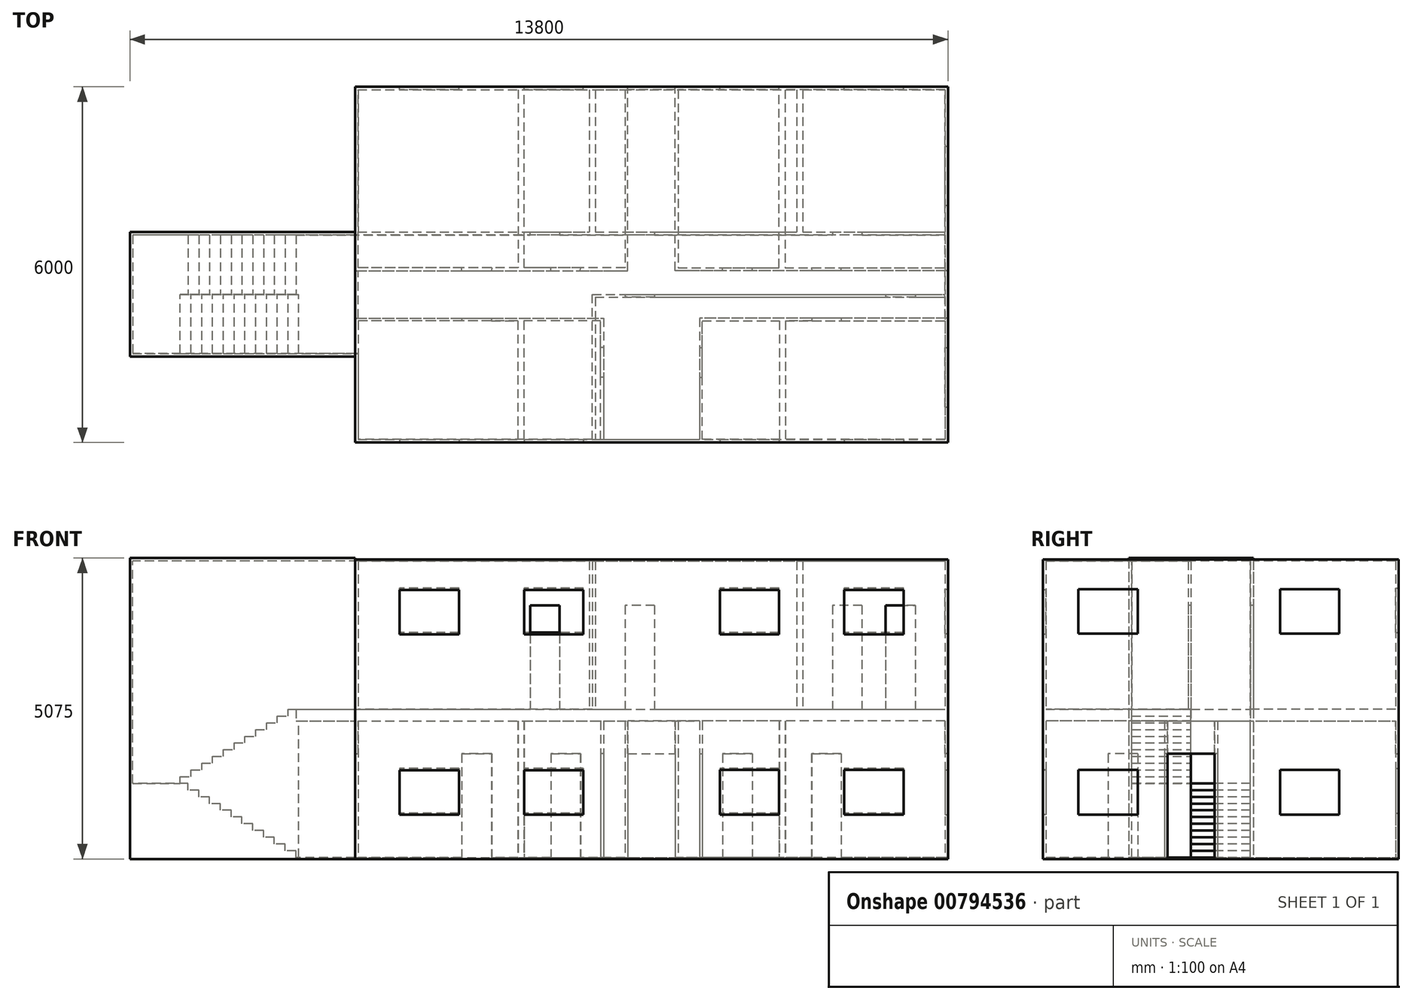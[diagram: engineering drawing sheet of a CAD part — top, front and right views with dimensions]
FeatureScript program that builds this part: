
annotation { "Feature Type Name" : "Feature", "Feature Type Description" : "" }
export const myFeature = defineFeature(function(context is Context, id is Id, definition is map)
    precondition{}
    {
        {
            var Q0;
            Q0=qCreatedBy(makeId("Top.planeOp"),FACE);
            var sketch = newSketch(context, id + "F0", { "sketchPlane" : qUnion([Q0])});
            skLineSegment(sketch, "E0.bottom", {"start": v(0, 0) * mm, "end": v(10000, 0) * mm});
            skLineSegment(sketch, "E0.top", {"start": v(0, 6000) * mm, "end": v(10000, 6000) * mm});
            skLineSegment(sketch, "E0.left", {"start": v(0, 0) * mm, "end": v(0, 6000) * mm});
            skLineSegment(sketch, "E0.right", {"start": v(10000, 0) * mm, "end": v(10000, 6000) * mm});
            skSolve(sketch);
        }
        {
            var Q0;
            Q0=qCreatedBy(makeId("Top.planeOp"),FACE);
            var sketch = newSketch(context, id + "F1", { "sketchPlane" : qUnion([Q0])});
            skLineSegment(sketch, "E1.bottom", {"start": v(0, 0) * mm, "end": v(5000, 0) * mm});
            skLineSegment(sketch, "E1.top", {"start": v(0, 6000) * mm, "end": v(4600, 6000) * mm});
            skLineSegment(sketch, "E1.left", {"start": v(0, 0) * mm, "end": v(0, 2100) * mm});
            skLineSegment(sketch, "E2", {"start": v(0, 2900) * mm, "end": v(1800, 2900) * mm});
            skLineSegment(sketch, "E3", {"start": v(0, 2100) * mm, "end": v(1800, 2100) * mm});
            skLineSegment(sketch, "E4", {"start": v(2800, 2900) * mm, "end": v(2800, 6000) * mm});
            skLineSegment(sketch, "E5", {"start": v(2792.35, 2100) * mm, "end": v(2792.35, 0) * mm});
            skLineSegment(sketch, "E6", {"start": v(2800, 2900) * mm, "end": v(3300, 2900) * mm});
            skLineSegment(sketch, "E7", {"start": v(4600, 2900) * mm, "end": v(4600, 6000) * mm});
            skLineSegment(sketch, "E8", {"start": v(2792.35, 2100) * mm, "end": v(4192.35, 2100) * mm});
            skLineSegment(sketch, "E9", {"start": v(4192.35, 2100) * mm, "end": v(4192.35, 1600) * mm});
            skPoint(sketch, "E10", {"position": v(1800, 2900) * mm});
            skPoint(sketch, "E11", {"position": v(2300, 2900) * mm});
            skPoint(sketch, "E12", {"position": v(1800, 2100) * mm});
            skPoint(sketch, "E13", {"position": v(2300, 2100) * mm});
            skPoint(sketch, "E14", {"position": v(4192.35, 1600) * mm});
            skPoint(sketch, "E15", {"position": v(3300, 2900) * mm});
            skPoint(sketch, "E16", {"position": v(3800, 2900) * mm});
            skPoint(sketch, "E17", {"position": v(4192.35, 1100) * mm});
            skLineSegment(sketch, "E18.trimOffspring", {"start": v(2300, 2900) * mm, "end": v(2800, 2900) * mm});
            skLineSegment(sketch, "E19.trimOffspring", {"start": v(2300, 2100) * mm, "end": v(2792.35, 2100) * mm});
            skLineSegment(sketch, "E20.trimOffspring", {"start": v(3800, 2900) * mm, "end": v(4600, 2900) * mm});
            skLineSegment(sketch, "E21.trimOffspring", {"start": v(4192.35, 1100) * mm, "end": v(4192.35, 0) * mm});
            skLineSegment(sketch, "E22.trimOffspring", {"start": v(0, 2900) * mm, "end": v(0, 6000) * mm});
            skLineSegment(sketch, "E23", {"start": v(1800, 2100) * mm, "end": v(1800, 2050) * mm});
            skLineSegment(sketch, "E24", {"start": v(1800, 2050) * mm, "end": v(50, 2050) * mm});
            skLineSegment(sketch, "E25", {"start": v(50, 2050) * mm, "end": v(50, 50) * mm});
            skLineSegment(sketch, "E26", {"start": v(50, 50) * mm, "end": v(2742.35, 50) * mm});
            skLineSegment(sketch, "E27", {"start": v(2300, 2100) * mm, "end": v(2300, 2050) * mm});
            skLineSegment(sketch, "E28", {"start": v(2300, 2050) * mm, "end": v(2742.35, 2050) * mm});
            skLineSegment(sketch, "E29", {"start": v(2742.35, 2050) * mm, "end": v(2742.35, 50) * mm});
            skLineSegment(sketch, "E30", {"start": v(4192.35, 1600) * mm, "end": v(4142.35, 1600) * mm});
            skLineSegment(sketch, "E31", {"start": v(4142.35, 1600) * mm, "end": v(4142.35, 2050) * mm});
            skLineSegment(sketch, "E32", {"start": v(4142.35, 2050) * mm, "end": v(2842.35, 2050) * mm});
            skLineSegment(sketch, "E33", {"start": v(2842.35, 2050) * mm, "end": v(2842.35, 50) * mm});
            skLineSegment(sketch, "E34", {"start": v(2842.35, 50) * mm, "end": v(4142.35, 50) * mm});
            skLineSegment(sketch, "E35", {"start": v(4192.35, 1100) * mm, "end": v(4142.35, 1100) * mm});
            skLineSegment(sketch, "E36", {"start": v(4142.35, 50) * mm, "end": v(4142.35, 1100) * mm});
            skLineSegment(sketch, "E37", {"start": v(4192.35, 50) * mm, "end": v(5000, 50) * mm});
            skLineSegment(sketch, "E38", {"start": v(5000, 0) * mm, "end": v(5000, 50) * mm});
            skLineSegment(sketch, "E39", {"start": v(1800, 2900) * mm, "end": v(1800, 2950) * mm});
            skLineSegment(sketch, "E40", {"start": v(1800, 2950) * mm, "end": v(50, 2950) * mm});
            skLineSegment(sketch, "E41", {"start": v(50, 2950) * mm, "end": v(50, 5950) * mm});
            skLineSegment(sketch, "E42", {"start": v(50, 5950) * mm, "end": v(2750, 5950) * mm});
            skLineSegment(sketch, "E43", {"start": v(2750, 5950) * mm, "end": v(2750, 2950) * mm});
            skLineSegment(sketch, "E44", {"start": v(2750, 2950) * mm, "end": v(2303.7, 2950) * mm});
            skLineSegment(sketch, "E45", {"start": v(2303.7, 2950) * mm, "end": v(2300, 2900) * mm});
            skLineSegment(sketch, "E46", {"start": v(3300, 2900) * mm, "end": v(3300, 2950) * mm});
            skLineSegment(sketch, "E47", {"start": v(3300, 2950) * mm, "end": v(2850, 2950) * mm});
            skLineSegment(sketch, "E48", {"start": v(2850, 2950) * mm, "end": v(2850, 5950) * mm});
            skLineSegment(sketch, "E49", {"start": v(2850, 5950) * mm, "end": v(4550, 5950) * mm});
            skLineSegment(sketch, "E50", {"start": v(4550, 5950) * mm, "end": v(4550, 2950) * mm});
            skLineSegment(sketch, "E51", {"start": v(4550, 2950) * mm, "end": v(3800.9, 2950) * mm});
            skLineSegment(sketch, "E52", {"start": v(3800, 2900) * mm, "end": v(3800.9, 2950) * mm});
            skSolve(sketch);
        }
        {
            var Q0;
            Q0=qSketchRegion(id+"F0",true);
            extrude(context, id + "F2", {"entities" : qUnion([Q0]), "oppositeDirection" : true, "depth" : 25 * mm, "offsetDistance" : 25 * mm});
        }
        {
            var Q0;
            Q0=qSketchRegion(id+"F1",true);
            extrude(context, id + "F3", {"entities" : qUnion([Q0]), "operationType" : NewBodyOperationType.ADD, "depth" : 2500 * mm, "offsetDistance" : 25 * mm});
        }
        {
            var Q0;
            Q0=qCreatedBy(makeId("Top.planeOp"),FACE);
            cPlane(context, id + "F4", {"entities" : qUnion([Q0]), "cplaneType" : CPlaneType.OFFSET, "offset" : 2500 * mm, "width" : 150 * mm, "height" : 150 * mm});
        }
        {
            var Q0;
            Q0=qCreatedBy(id+"F4.planeOp",FACE);
            var sketch = newSketch(context, id + "F5", { "sketchPlane" : qUnion([Q0])});
            skLineSegment(sketch, "E53.bottom", {"start": v(0, 0) * mm, "end": v(10000, 0) * mm});
            skLineSegment(sketch, "E53.top", {"start": v(0, 6000) * mm, "end": v(10000, 6000) * mm});
            skLineSegment(sketch, "E53.left", {"start": v(0, 0) * mm, "end": v(0, 6000) * mm});
            skLineSegment(sketch, "E53.right", {"start": v(10000, 0) * mm, "end": v(10000, 6000) * mm});
            skSolve(sketch);
        }
        {
            var Q0;
            Q0=qSketchRegion(id+"F5",true);
            extrude(context, id + "F6", {"entities" : qUnion([Q0]), "operationType" : NewBodyOperationType.ADD, "oppositeDirection" : true, "depth" : 200 * mm, "offsetDistance" : 25 * mm});
        }
        {
            var Q0;
            Q0=qCreatedBy(id+"F4.planeOp",FACE);
            var sketch = newSketch(context, id + "F7", { "sketchPlane" : qUnion([Q0])});
            skLineSegment(sketch, "E54.bottom", {"start": v(0, 0) * mm, "end": v(5000, 0) * mm});
            skLineSegment(sketch, "E54.top", {"start": v(0, 6000) * mm, "end": v(4600, 6000) * mm});
            skLineSegment(sketch, "E54.left", {"start": v(0, 0) * mm, "end": v(0, 2100) * mm});
            skLineSegment(sketch, "E55", {"start": v(0, 2900) * mm, "end": v(1800, 2900) * mm});
            skLineSegment(sketch, "E56", {"start": v(0, 2100) * mm, "end": v(1800, 2100) * mm});
            skLineSegment(sketch, "E57", {"start": v(2800, 2900) * mm, "end": v(2800, 6000) * mm});
            skLineSegment(sketch, "E58", {"start": v(2792.35, 2100) * mm, "end": v(2792.35, 0) * mm});
            skLineSegment(sketch, "E59", {"start": v(2800, 2900) * mm, "end": v(3300, 2900) * mm});
            skLineSegment(sketch, "E60", {"start": v(4600, 2900) * mm, "end": v(4600, 6000) * mm});
            skLineSegment(sketch, "E61", {"start": v(2792.35, 2100) * mm, "end": v(4192.35, 2100) * mm});
            skLineSegment(sketch, "E62", {"start": v(4192.35, 2100) * mm, "end": v(4192.35, 1600) * mm});
            skPoint(sketch, "E63", {"position": v(1800, 2900) * mm});
            skPoint(sketch, "E64", {"position": v(2300, 2900) * mm});
            skPoint(sketch, "E65", {"position": v(1800, 2100) * mm});
            skPoint(sketch, "E66", {"position": v(2300, 2100) * mm});
            skPoint(sketch, "E67", {"position": v(4192.35, 1600) * mm});
            skPoint(sketch, "E68", {"position": v(3300, 2900) * mm});
            skPoint(sketch, "E69", {"position": v(3800, 2900) * mm});
            skPoint(sketch, "E70", {"position": v(4192.35, 1100) * mm});
            skLineSegment(sketch, "E71.trimOffspring", {"start": v(2300, 2900) * mm, "end": v(2800, 2900) * mm});
            skLineSegment(sketch, "E72.trimOffspring", {"start": v(2300, 2100) * mm, "end": v(2792.35, 2100) * mm});
            skLineSegment(sketch, "E73.trimOffspring", {"start": v(3800, 2900) * mm, "end": v(4600, 2900) * mm});
            skLineSegment(sketch, "E74.trimOffspring", {"start": v(4192.35, 1100) * mm, "end": v(4192.35, 0) * mm});
            skLineSegment(sketch, "E75.trimOffspring", {"start": v(0, 2900) * mm, "end": v(0, 6000) * mm});
            skLineSegment(sketch, "E76", {"start": v(1800, 2100) * mm, "end": v(1800, 2050) * mm});
            skLineSegment(sketch, "E77", {"start": v(1800, 2050) * mm, "end": v(50, 2050) * mm});
            skLineSegment(sketch, "E78", {"start": v(50, 2050) * mm, "end": v(50, 50) * mm});
            skLineSegment(sketch, "E79", {"start": v(50, 50) * mm, "end": v(2742.35, 50) * mm});
            skLineSegment(sketch, "E80", {"start": v(2300, 2100) * mm, "end": v(2300, 2050) * mm});
            skLineSegment(sketch, "E81", {"start": v(2300, 2050) * mm, "end": v(2742.35, 2050) * mm});
            skLineSegment(sketch, "E82", {"start": v(2742.35, 2050) * mm, "end": v(2742.35, 50) * mm});
            skLineSegment(sketch, "E83", {"start": v(4192.35, 1600) * mm, "end": v(4142.35, 1600) * mm});
            skLineSegment(sketch, "E84", {"start": v(4142.35, 1600) * mm, "end": v(4142.35, 2050) * mm});
            skLineSegment(sketch, "E85", {"start": v(4142.35, 2050) * mm, "end": v(2842.35, 2050) * mm});
            skLineSegment(sketch, "E86", {"start": v(2842.35, 2050) * mm, "end": v(2842.35, 50) * mm});
            skLineSegment(sketch, "E87", {"start": v(2842.35, 50) * mm, "end": v(4142.35, 50) * mm});
            skLineSegment(sketch, "E88", {"start": v(4192.35, 1100) * mm, "end": v(4142.35, 1100) * mm});
            skLineSegment(sketch, "E89", {"start": v(4142.35, 50) * mm, "end": v(4142.35, 1100) * mm});
            skLineSegment(sketch, "E90", {"start": v(4192.35, 50) * mm, "end": v(5000, 50) * mm});
            skLineSegment(sketch, "E91", {"start": v(5000, 0) * mm, "end": v(5000, 50) * mm});
            skLineSegment(sketch, "E92", {"start": v(1800, 2900) * mm, "end": v(1800, 2950) * mm});
            skLineSegment(sketch, "E93", {"start": v(1800, 2950) * mm, "end": v(50, 2950) * mm});
            skLineSegment(sketch, "E94", {"start": v(50, 2950) * mm, "end": v(50, 5950) * mm});
            skLineSegment(sketch, "E95", {"start": v(50, 5950) * mm, "end": v(2750, 5950) * mm});
            skLineSegment(sketch, "E96", {"start": v(2750, 5950) * mm, "end": v(2750, 2950) * mm});
            skLineSegment(sketch, "E97", {"start": v(2750, 2950) * mm, "end": v(2303.7, 2950) * mm});
            skLineSegment(sketch, "E98", {"start": v(2303.7, 2950) * mm, "end": v(2300, 2900) * mm});
            skLineSegment(sketch, "E99", {"start": v(3300, 2900) * mm, "end": v(3300, 2950) * mm});
            skLineSegment(sketch, "E100", {"start": v(3300, 2950) * mm, "end": v(2850, 2950) * mm});
            skLineSegment(sketch, "E101", {"start": v(2850, 2950) * mm, "end": v(2850, 5950) * mm});
            skLineSegment(sketch, "E102", {"start": v(2850, 5950) * mm, "end": v(4550, 5950) * mm});
            skLineSegment(sketch, "E103", {"start": v(4550, 5950) * mm, "end": v(4550, 2950) * mm});
            skLineSegment(sketch, "E104", {"start": v(4550, 2950) * mm, "end": v(3800.9, 2950) * mm});
            skLineSegment(sketch, "E105", {"start": v(3800, 2900) * mm, "end": v(3800.9, 2950) * mm});
            skLineSegment(sketch, "E106", {"start": v(0, 2900) * mm, "end": v(0, 2100) * mm});
            skLineSegment(sketch, "E107", {"start": v(50, 2050) * mm, "end": v(50, 2950) * mm});
            skLineSegment(sketch, "E108", {"start": v(1800, 2050) * mm, "end": v(2300, 2050) * mm});
            skLineSegment(sketch, "E109", {"start": v(2300, 2100) * mm, "end": v(1800, 2100) * mm});
            skLineSegment(sketch, "E110", {"start": v(1800, 2900) * mm, "end": v(2300, 2900) * mm});
            skLineSegment(sketch, "E111", {"start": v(1800, 2950) * mm, "end": v(2303.7, 2950) * mm});
            skLineSegment(sketch, "E112", {"start": v(3300, 2900) * mm, "end": v(3800, 2900) * mm});
            skLineSegment(sketch, "E113", {"start": v(3800.9, 2950) * mm, "end": v(3300, 2950) * mm});
            skLineSegment(sketch, "E114", {"start": v(4192.35, 1600) * mm, "end": v(4192.35, 1100) * mm});
            skLineSegment(sketch, "E115", {"start": v(4142.35, 1100) * mm, "end": v(4142.35, 1600) * mm});
            skLineSegment(sketch, "E116", {"start": v(4600, 6000) * mm, "end": v(5000, 6000) * mm});
            skLineSegment(sketch, "E117", {"start": v(5000, 6000) * mm, "end": v(5000, 5950) * mm});
            skLineSegment(sketch, "E118", {"start": v(5000, 5950) * mm, "end": v(4550, 5950) * mm});
            skSolve(sketch);
        }
        {
            var Q0;
            Q0=qSketchRegion(id+"F7",true);
            extrude(context, id + "F8", {"entities" : qUnion([Q0]), "operationType" : NewBodyOperationType.ADD, "oppositeDirection" : true, "depth" : 750 * mm, "offsetDistance" : 25 * mm});
        }
        {
            var Q0;
            Q0=makeQuery(id+"F2.opExtrude","SWEPT_BODY",BODY,{"disambiguationData":[OSD([sQuery(id+"F0.wireOp",EDGE,"E0.bottom"),sQuery(id+"F0.wireOp",EDGE,"E0.top"),sQuery(id+"F0.wireOp",EDGE,"E0.left"),sQuery(id+"F0.wireOp",EDGE,"E0.right")])]});
            var Q1;
            Q1=makeQuery(id+"F3.opExtrude","SWEPT_FACE",FACE,{"disambiguationData":[OSD([sQuery(id+"F1.wireOp",EDGE,"E38")])]});
            mirror(context, id + "F9", {"operationType" : NewBodyOperationType.ADD, "entities" : qUnion([Q0]), "mirrorPlane" : qUnion([Q1])});
        }
        {
            var Q0;
            Q0=qCreatedBy(makeId("Front.planeOp"),FACE);
            cPlane(context, id + "F10", {"entities" : qUnion([Q0]), "cplaneType" : CPlaneType.OFFSET, "offset" : 2500 * mm, "oppositeDirection" : true, "width" : 150 * mm, "height" : 150 * mm});
        }
        {
            var Q0;
            Q0=qCreatedBy(id+"F10.planeOp",FACE);
            var sketch = newSketch(context, id + "F11", { "sketchPlane" : qUnion([Q0])});
            skLineSegment(sketch, "E119.bottom", {"start": v(-1000, 0) * mm, "end": v(-3000, 0) * mm});
            skLineSegment(sketch, "E119.right", {"start": v(-3000, 0) * mm, "end": v(-3000, 1250) * mm});
            skLineSegment(sketch, "E120", {"start": v(-1000, 0) * mm, "end": v(-3000, 1250) * mm});
            skLineSegment(sketch, "E121.bottom", {"start": v(-1000, 0) * mm, "end": v(-1181.82, 0) * mm});
            skLineSegment(sketch, "E121.top", {"start": v(-1000, 113.64) * mm, "end": v(-1181.82, 113.64) * mm});
            skLineSegment(sketch, "E121.left", {"start": v(-1000, 0) * mm, "end": v(-1000, 113.64) * mm});
            skLineSegment(sketch, "E121.right", {"start": v(-1181.82, 0) * mm, "end": v(-1181.82, 113.64) * mm});
            skLineSegment(sketch, "E122.bottom", {"start": v(-1181.82, 0) * mm, "end": v(-1363.64, 0) * mm});
            skLineSegment(sketch, "E122.top", {"start": v(-1181.82, 227.27) * mm, "end": v(-1363.64, 227.27) * mm});
            skLineSegment(sketch, "E122.left", {"start": v(-1181.82, 0) * mm, "end": v(-1181.82, 227.27) * mm});
            skLineSegment(sketch, "E122.right", {"start": v(-1363.64, 0) * mm, "end": v(-1363.64, 227.27) * mm});
            skLineSegment(sketch, "E123.bottom", {"start": v(-1363.64, 0) * mm, "end": v(-1545.45, 0) * mm});
            skLineSegment(sketch, "E123.top", {"start": v(-1363.64, 340.9) * mm, "end": v(-1545.45, 340.9) * mm});
            skLineSegment(sketch, "E123.left", {"start": v(-1363.64, 0) * mm, "end": v(-1363.64, 340.9) * mm});
            skLineSegment(sketch, "E123.right", {"start": v(-1545.45, 0) * mm, "end": v(-1545.45, 340.9) * mm});
            skLineSegment(sketch, "E124.bottom", {"start": v(-1545.45, 0) * mm, "end": v(-1727.27, 0) * mm});
            skLineSegment(sketch, "E124.top", {"start": v(-1545.45, 454.55) * mm, "end": v(-1727.27, 454.55) * mm});
            skLineSegment(sketch, "E124.left", {"start": v(-1545.45, 0) * mm, "end": v(-1545.45, 454.55) * mm});
            skLineSegment(sketch, "E124.right", {"start": v(-1727.27, 0) * mm, "end": v(-1727.27, 454.55) * mm});
            skLineSegment(sketch, "E125.bottom", {"start": v(-1727.27, 0) * mm, "end": v(-1909.1, 0) * mm});
            skLineSegment(sketch, "E125.top", {"start": v(-1727.27, 568.18) * mm, "end": v(-1909.1, 568.18) * mm});
            skLineSegment(sketch, "E125.left", {"start": v(-1727.27, 0) * mm, "end": v(-1727.27, 568.18) * mm});
            skLineSegment(sketch, "E125.right", {"start": v(-1909.1, 0) * mm, "end": v(-1909.1, 568.18) * mm});
            skLineSegment(sketch, "E126.bottom", {"start": v(-1909.1, 0) * mm, "end": v(-2090.9, 0) * mm});
            skLineSegment(sketch, "E126.top", {"start": v(-1909.1, 681.81) * mm, "end": v(-2090.9, 681.81) * mm});
            skLineSegment(sketch, "E126.left", {"start": v(-1909.1, 0) * mm, "end": v(-1909.1, 681.81) * mm});
            skLineSegment(sketch, "E126.right", {"start": v(-2090.9, 0) * mm, "end": v(-2090.9, 681.81) * mm});
            skLineSegment(sketch, "E127.bottom", {"start": v(-2090.9, 0) * mm, "end": v(-2272.72, 0) * mm});
            skLineSegment(sketch, "E127.top", {"start": v(-2090.9, 795.45) * mm, "end": v(-2272.72, 795.45) * mm});
            skLineSegment(sketch, "E127.left", {"start": v(-2090.9, 0) * mm, "end": v(-2090.9, 795.45) * mm});
            skLineSegment(sketch, "E127.right", {"start": v(-2272.72, 0) * mm, "end": v(-2272.72, 795.45) * mm});
            skLineSegment(sketch, "E128.bottom", {"start": v(-2272.72, 0) * mm, "end": v(-2454.54, 0) * mm});
            skLineSegment(sketch, "E128.top", {"start": v(-2272.72, 909.09) * mm, "end": v(-2454.54, 909.09) * mm});
            skLineSegment(sketch, "E128.left", {"start": v(-2272.72, 0) * mm, "end": v(-2272.72, 909.09) * mm});
            skLineSegment(sketch, "E128.right", {"start": v(-2454.54, 0) * mm, "end": v(-2454.54, 909.09) * mm});
            skLineSegment(sketch, "E129.bottom", {"start": v(-2454.54, 0) * mm, "end": v(-2636.36, 0) * mm});
            skLineSegment(sketch, "E129.top", {"start": v(-2454.54, 1022.72) * mm, "end": v(-2636.36, 1022.72) * mm});
            skLineSegment(sketch, "E129.left", {"start": v(-2454.54, 0) * mm, "end": v(-2454.54, 1022.72) * mm});
            skLineSegment(sketch, "E129.right", {"start": v(-2636.36, 0) * mm, "end": v(-2636.36, 1022.72) * mm});
            skLineSegment(sketch, "E130.bottom", {"start": v(-2636.36, 0) * mm, "end": v(-2818.17, 0) * mm});
            skLineSegment(sketch, "E130.top", {"start": v(-2636.36, 1136.36) * mm, "end": v(-2818.17, 1136.36) * mm});
            skLineSegment(sketch, "E130.left", {"start": v(-2636.36, 0) * mm, "end": v(-2636.36, 1136.36) * mm});
            skLineSegment(sketch, "E130.right", {"start": v(-2818.17, 0) * mm, "end": v(-2818.17, 1136.36) * mm});
            skLineSegment(sketch, "E131.bottom", {"start": v(-3000, 0) * mm, "end": v(-3750, 0) * mm});
            skLineSegment(sketch, "E131.top", {"start": v(-3000, 1250) * mm, "end": v(-3750, 1250) * mm});
            skLineSegment(sketch, "E131.right", {"start": v(-3750, 0) * mm, "end": v(-3750, 1250) * mm});
            skLineSegment(sketch, "E132.bottom", {"start": v(-2818.17, 0) * mm, "end": v(-3000, 0) * mm});
            skLineSegment(sketch, "E132.top", {"start": v(-2818.17, 1250) * mm, "end": v(-3000, 1250) * mm});
            skLineSegment(sketch, "E132.left", {"start": v(-2818.17, 0) * mm, "end": v(-2818.17, 1250) * mm});
            skSolve(sketch);
        }
        {
            var Q0;
            Q0=qSketchRegion(id+"F11",true);
            extrude(context, id + "F12", {"entities" : qUnion([Q0]), "operationType" : NewBodyOperationType.ADD, "oppositeDirection" : true, "depth" : 1000 * mm, "offsetDistance" : 25 * mm});
        }
        {
            var Q0;
            Q0=qCreatedBy(id+"F10.planeOp",FACE);
            var sketch = newSketch(context, id + "F13", { "sketchPlane" : qUnion([Q0])});
            skLineSegment(sketch, "E133.bottom", {"start": v(-3750, 0) * mm, "end": v(-2950, 0) * mm});
            skLineSegment(sketch, "E133.top", {"start": v(-3750, 1250) * mm, "end": v(-2950, 1250) * mm});
            skLineSegment(sketch, "E133.left", {"start": v(-3750, 0) * mm, "end": v(-3750, 1250) * mm});
            skLineSegment(sketch, "E133.right", {"start": v(-2950, 0) * mm, "end": v(-2950, 1250) * mm});
            skLineSegment(sketch, "E134", {"start": v(-2950, 1250) * mm, "end": v(-950, 1250) * mm});
            skLineSegment(sketch, "E135", {"start": v(-2950, 0) * mm, "end": v(-950, 0) * mm});
            skLineSegment(sketch, "E136", {"start": v(-950, 0) * mm, "end": v(-950, 1250) * mm});
            skLineSegment(sketch, "E137", {"start": v(-950, 1250) * mm, "end": v(-950, 2500) * mm});
            skLineSegment(sketch, "E138", {"start": v(-2950, 1250) * mm, "end": v(-950, 2500) * mm});
            skLineSegment(sketch, "E139.bottom", {"start": v(-2950, 1250) * mm, "end": v(-2768.18, 1250) * mm});
            skLineSegment(sketch, "E139.top", {"start": v(-2950, 1363.64) * mm, "end": v(-2768.18, 1363.64) * mm});
            skLineSegment(sketch, "E139.left", {"start": v(-2950, 1250) * mm, "end": v(-2950, 1363.64) * mm});
            skLineSegment(sketch, "E139.right", {"start": v(-2768.18, 1250) * mm, "end": v(-2768.18, 1363.64) * mm});
            skLineSegment(sketch, "E140.bottom", {"start": v(-2768.18, 1250) * mm, "end": v(-2586.36, 1250) * mm});
            skLineSegment(sketch, "E140.top", {"start": v(-2768.18, 1477.27) * mm, "end": v(-2586.36, 1477.27) * mm});
            skLineSegment(sketch, "E140.left", {"start": v(-2768.18, 1250) * mm, "end": v(-2768.18, 1477.27) * mm});
            skLineSegment(sketch, "E140.right", {"start": v(-2586.36, 1250) * mm, "end": v(-2586.36, 1477.27) * mm});
            skLineSegment(sketch, "E141.bottom", {"start": v(-2586.36, 1250) * mm, "end": v(-2404.55, 1250) * mm});
            skLineSegment(sketch, "E141.top", {"start": v(-2586.36, 1590.9) * mm, "end": v(-2404.55, 1590.9) * mm});
            skLineSegment(sketch, "E141.left", {"start": v(-2586.36, 1250) * mm, "end": v(-2586.36, 1590.9) * mm});
            skLineSegment(sketch, "E141.right", {"start": v(-2404.55, 1250) * mm, "end": v(-2404.55, 1590.9) * mm});
            skLineSegment(sketch, "E142.bottom", {"start": v(-2404.55, 1250) * mm, "end": v(-2222.74, 1250) * mm});
            skLineSegment(sketch, "E142.top", {"start": v(-2404.55, 1704.54) * mm, "end": v(-2222.74, 1704.54) * mm});
            skLineSegment(sketch, "E142.left", {"start": v(-2404.55, 1250) * mm, "end": v(-2404.55, 1704.54) * mm});
            skLineSegment(sketch, "E142.right", {"start": v(-2222.74, 1250) * mm, "end": v(-2222.74, 1704.54) * mm});
            skLineSegment(sketch, "E143.bottom", {"start": v(-2222.74, 1250) * mm, "end": v(-2040.92, 1250) * mm});
            skLineSegment(sketch, "E143.top", {"start": v(-2222.74, 1818.18) * mm, "end": v(-2040.92, 1818.18) * mm});
            skLineSegment(sketch, "E143.left", {"start": v(-2222.74, 1250) * mm, "end": v(-2222.74, 1818.18) * mm});
            skLineSegment(sketch, "E143.right", {"start": v(-2040.92, 1250) * mm, "end": v(-2040.92, 1818.18) * mm});
            skLineSegment(sketch, "E144.bottom", {"start": v(-2040.92, 1250) * mm, "end": v(-1859.1, 1250) * mm});
            skLineSegment(sketch, "E144.top", {"start": v(-2040.92, 1931.81) * mm, "end": v(-1859.1, 1931.81) * mm});
            skLineSegment(sketch, "E144.left", {"start": v(-2040.92, 1250) * mm, "end": v(-2040.92, 1931.81) * mm});
            skLineSegment(sketch, "E144.right", {"start": v(-1859.1, 1250) * mm, "end": v(-1859.1, 1931.81) * mm});
            skLineSegment(sketch, "E145.bottom", {"start": v(-1859.1, 1250) * mm, "end": v(-1677.29, 1250) * mm});
            skLineSegment(sketch, "E145.top", {"start": v(-1859.1, 2045.44) * mm, "end": v(-1677.29, 2045.44) * mm});
            skLineSegment(sketch, "E145.left", {"start": v(-1859.1, 1250) * mm, "end": v(-1859.1, 2045.44) * mm});
            skLineSegment(sketch, "E145.right", {"start": v(-1677.29, 1250) * mm, "end": v(-1677.29, 2045.44) * mm});
            skLineSegment(sketch, "E146.bottom", {"start": v(-1677.29, 1250) * mm, "end": v(-1495.47, 1250) * mm});
            skLineSegment(sketch, "E146.top", {"start": v(-1677.29, 2159.08) * mm, "end": v(-1495.47, 2159.08) * mm});
            skLineSegment(sketch, "E146.left", {"start": v(-1677.29, 1250) * mm, "end": v(-1677.29, 2159.08) * mm});
            skLineSegment(sketch, "E146.right", {"start": v(-1495.47, 1250) * mm, "end": v(-1495.47, 2159.08) * mm});
            skLineSegment(sketch, "E147.bottom", {"start": v(-1495.47, 1250) * mm, "end": v(-1313.65, 1250) * mm});
            skLineSegment(sketch, "E147.top", {"start": v(-1495.47, 2272.72) * mm, "end": v(-1313.65, 2272.72) * mm});
            skLineSegment(sketch, "E147.left", {"start": v(-1495.47, 1250) * mm, "end": v(-1495.47, 2272.72) * mm});
            skLineSegment(sketch, "E147.right", {"start": v(-1313.65, 1250) * mm, "end": v(-1313.65, 2272.72) * mm});
            skLineSegment(sketch, "E148.bottom", {"start": v(-1313.65, 1250) * mm, "end": v(-1131.84, 1250) * mm});
            skLineSegment(sketch, "E148.top", {"start": v(-1313.65, 2386.35) * mm, "end": v(-1131.84, 2386.35) * mm});
            skLineSegment(sketch, "E148.left", {"start": v(-1313.65, 1250) * mm, "end": v(-1313.65, 2386.35) * mm});
            skLineSegment(sketch, "E148.right", {"start": v(-1131.84, 1250) * mm, "end": v(-1131.84, 2386.35) * mm});
            skLineSegment(sketch, "E149.bottom", {"start": v(-1131.84, 1250) * mm, "end": v(-950, 1250) * mm});
            skLineSegment(sketch, "E149.top", {"start": v(-1131.84, 2500) * mm, "end": v(-950, 2500) * mm});
            skLineSegment(sketch, "E149.left", {"start": v(-1131.84, 1250) * mm, "end": v(-1131.84, 2500) * mm});
            skSolve(sketch);
        }
        {
            var Q0;
            Q0=qSketchRegion(id+"F13",true);
            extrude(context, id + "F14", {"entities" : qUnion([Q0]), "operationType" : NewBodyOperationType.ADD, "depth" : 1000 * mm, "offsetDistance" : 25 * mm});
        }
        {
            var Q0;
            Q0=makeQuery(id+"F8.boolean.opBoolean","MERGE",FACE,{"derivedFrom":[makeQuery(id+"F6.boolean.opBoolean","MERGE",FACE,{"derivedFrom":[makeQuery(id+"F3.boolean.opBoolean","MERGE",FACE,{"derivedFrom":[makeQuery(id+"F2.opExtrude","SWEPT_FACE",FACE,{"disambiguationData":[OSD([sQuery(id+"F0.wireOp",EDGE,"E0.left")])]}),makeQuery(id+"F3.opExtrude","SWEPT_FACE",FACE,{"disambiguationData":[OSD([sQuery(id+"F1.wireOp",EDGE,"E1.left")])]}),makeQuery(id+"F3.opExtrude","SWEPT_FACE",FACE,{"disambiguationData":[OSD([sQuery(id+"F1.wireOp",EDGE,"E22.trimOffspring")])]})]}),makeQuery(id+"F6.opExtrude","SWEPT_FACE",FACE,{"disambiguationData":[OSD([sQuery(id+"F5.wireOp",EDGE,"E53.left")])]})]}),makeQuery(id+"F8.opExtrude","SWEPT_FACE",FACE,{"disambiguationData":[OSD([sQuery(id+"F7.wireOp",EDGE,"E54.left"),sQuery(id+"F7.wireOp",EDGE,"E75.trimOffspring"),sQuery(id+"F7.wireOp",EDGE,"E106")])]})]});
            var sketch = newSketch(context, id + "F15", { "sketchPlane" : qUnion([Q0])});
            skLineSegment(sketch, "E150.top", {"start": v(-1500, 2500) * mm, "end": v(-3500, 2500) * mm});
            skLineSegment(sketch, "E151", {"start": v(-3500, 2500) * mm, "end": v(-3500, 2300) * mm});
            skLineSegment(sketch, "E152", {"start": v(-1500, 2500) * mm, "end": v(-1500, 2300) * mm});
            skLineSegment(sketch, "E153", {"start": v(-1500, 2300) * mm, "end": v(-3500, 2300) * mm});
            skSolve(sketch);
        }
        {
            var Q0;
            Q0=qSketchRegion(id+"F15",true);
            extrude(context, id + "F16", {"entities" : qUnion([Q0]), "operationType" : NewBodyOperationType.ADD, "depth" : 1000 * mm, "offsetDistance" : 25 * mm});
        }
        {
            var Q0;
            Q0=makeQuery(id+"F14.boolean.opBoolean","MERGE",FACE,{"derivedFrom":[makeQuery(id+"F12.opExtrude","SWEPT_FACE",FACE,{"disambiguationData":[OSD([sQuery(id+"F11.wireOp",EDGE,"E131.right")])]}),makeQuery(id+"F14.opExtrude","SWEPT_FACE",FACE,{"disambiguationData":[OSD([sQuery(id+"F13.wireOp",EDGE,"E133.left")])]})]});
            var sketch = newSketch(context, id + "F17", { "sketchPlane" : qUnion([Q0])});
            skLineSegment(sketch, "E154.bottom", {"start": v(-3500, 0) * mm, "end": v(-1500, 0) * mm});
            skLineSegment(sketch, "E154.top", {"start": v(-3500, 5000) * mm, "end": v(-1500, 5000) * mm});
            skLineSegment(sketch, "E154.left", {"start": v(-3500, 0) * mm, "end": v(-3500, 5000) * mm});
            skLineSegment(sketch, "E154.right", {"start": v(-1500, 0) * mm, "end": v(-1500, 5000) * mm});
            skLineSegment(sketch, "E155.bottom", {"start": v(-3550, 5050) * mm, "end": v(-1450, 5050) * mm});
            skLineSegment(sketch, "E155.top", {"start": v(-3550, -25) * mm, "end": v(-1450, -25) * mm});
            skLineSegment(sketch, "E155.left", {"start": v(-3550, 5050) * mm, "end": v(-3550, -25) * mm});
            skLineSegment(sketch, "E155.right", {"start": v(-1450, 5050) * mm, "end": v(-1450, -25) * mm});
            skSolve(sketch);
        }
        {
            var Q0;
            Q0=qSketchRegion(id+"F17",true);
            extrude(context, id + "F18", {"entities" : qUnion([Q0]), "operationType" : NewBodyOperationType.ADD, "oppositeDirection" : true, "depth" : 3750 * mm, "offsetDistance" : 25 * mm});
        }
        {
            var Q0;
            Q0=makeQuery(id+"F18.boolean.opBoolean","MERGE",FACE,{"derivedFrom":[makeQuery(id+"F14.boolean.opBoolean","MERGE",FACE,{"derivedFrom":[makeQuery(id+"F12.opExtrude","SWEPT_FACE",FACE,{"disambiguationData":[OSD([sQuery(id+"F11.wireOp",EDGE,"E131.right")])]}),makeQuery(id+"F14.opExtrude","SWEPT_FACE",FACE,{"disambiguationData":[OSD([sQuery(id+"F13.wireOp",EDGE,"E133.left")])]})]}),makeQuery(id+"F18.opExtrude","CAP_FACE",FACE,{"disambiguationData":[OSD([sQuery(id+"F17.wireOp",EDGE,"E154.bottom"),sQuery(id+"F17.wireOp",EDGE,"E154.top"),sQuery(id+"F17.wireOp",EDGE,"E154.left"),sQuery(id+"F17.wireOp",EDGE,"E154.right"),sQuery(id+"F17.wireOp",EDGE,"E155.bottom"),sQuery(id+"F17.wireOp",EDGE,"E155.top"),sQuery(id+"F17.wireOp",EDGE,"E155.left"),sQuery(id+"F17.wireOp",EDGE,"E155.right")])],"isStart":true})]});
            var sketch = newSketch(context, id + "F19", { "sketchPlane" : qUnion([Q0])});
            skLineSegment(sketch, "E156.bottom", {"start": v(-3550, -25) * mm, "end": v(-1450, -25) * mm});
            skLineSegment(sketch, "E156.top", {"start": v(-3550, 5050) * mm, "end": v(-1450, 5050) * mm});
            skLineSegment(sketch, "E156.left", {"start": v(-3550, -25) * mm, "end": v(-3550, 5050) * mm});
            skLineSegment(sketch, "E156.right", {"start": v(-1450, -25) * mm, "end": v(-1450, 5050) * mm});
            skSolve(sketch);
        }
        {
            var Q0;
            Q0=qSketchRegion(id+"F19",true);
            extrude(context, id + "F20", {"entities" : qUnion([Q0]), "operationType" : NewBodyOperationType.ADD, "depth" : 50 * mm, "offsetDistance" : 25 * mm});
        }
        {
            var Q0;
            {var subQ0=sQuery(id+"F5.wireOp",EDGE,"E53.top");var subQ1=sQuery(id+"F1.wireOp",EDGE,"E1.top");Q0=makeQuery(id+"F16.boolean.opBoolean","MERGE",FACE,{"derivedFrom":[makeQuery(id+"F12.boolean.opBoolean","MERGE",FACE,{"derivedFrom":[makeQuery(id+"F6.boolean.opBoolean","MERGE",FACE,{"derivedFrom":[makeQuery(id+"F3.opExtrude","CAP_FACE",FACE,{"disambiguationData":[OSD([sQuery(id+"F1.wireOp",EDGE,"E1.bottom"),sQuery(id+"F1.wireOp",EDGE,"E1.left"),sQuery(id+"F1.wireOp",EDGE,"E3"),sQuery(id+"F1.wireOp",EDGE,"E8"),sQuery(id+"F1.wireOp",EDGE,"E9"),sQuery(id+"F1.wireOp",EDGE,"E19.trimOffspring"),sQuery(id+"F1.wireOp",EDGE,"E21.trimOffspring"),sQuery(id+"F1.wireOp",EDGE,"E23"),sQuery(id+"F1.wireOp",EDGE,"E24"),sQuery(id+"F1.wireOp",EDGE,"E25"),sQuery(id+"F1.wireOp",EDGE,"E26"),sQuery(id+"F1.wireOp",EDGE,"E27"),sQuery(id+"F1.wireOp",EDGE,"E28"),sQuery(id+"F1.wireOp",EDGE,"E29"),sQuery(id+"F1.wireOp",EDGE,"E30"),sQuery(id+"F1.wireOp",EDGE,"E31"),sQuery(id+"F1.wireOp",EDGE,"E32"),sQuery(id+"F1.wireOp",EDGE,"E33"),sQuery(id+"F1.wireOp",EDGE,"E34"),sQuery(id+"F1.wireOp",EDGE,"E35"),sQuery(id+"F1.wireOp",EDGE,"E36"),sQuery(id+"F1.wireOp",EDGE,"E37"),sQuery(id+"F1.wireOp",EDGE,"E38")])],"isStart":false}),makeQuery(id+"F3.opExtrude","CAP_FACE",FACE,{"disambiguationData":[OSD([subQ1,sQuery(id+"F1.wireOp",EDGE,"E2"),sQuery(id+"F1.wireOp",EDGE,"E6"),sQuery(id+"F1.wireOp",EDGE,"E7"),sQuery(id+"F1.wireOp",EDGE,"E18.trimOffspring"),sQuery(id+"F1.wireOp",EDGE,"E20.trimOffspring"),sQuery(id+"F1.wireOp",EDGE,"E22.trimOffspring"),sQuery(id+"F1.wireOp",EDGE,"E39"),sQuery(id+"F1.wireOp",EDGE,"E40"),sQuery(id+"F1.wireOp",EDGE,"E41"),sQuery(id+"F1.wireOp",EDGE,"E42"),sQuery(id+"F1.wireOp",EDGE,"E43"),sQuery(id+"F1.wireOp",EDGE,"E44"),sQuery(id+"F1.wireOp",EDGE,"E45"),sQuery(id+"F1.wireOp",EDGE,"E46"),sQuery(id+"F1.wireOp",EDGE,"E47"),sQuery(id+"F1.wireOp",EDGE,"E48"),sQuery(id+"F1.wireOp",EDGE,"E49"),sQuery(id+"F1.wireOp",EDGE,"E50"),sQuery(id+"F1.wireOp",EDGE,"E51"),sQuery(id+"F1.wireOp",EDGE,"E52")])],"isStart":false}),makeQuery(id+"F6.opExtrude","CAP_FACE",FACE,{"disambiguationData":[OSD([sQuery(id+"F5.wireOp",EDGE,"E53.bottom"),subQ0,sQuery(id+"F5.wireOp",EDGE,"E53.left"),sQuery(id+"F5.wireOp",EDGE,"E53.right")])],"isStart":true})]}),makeQuery(id+"F12.opExtrude","SWEPT_FACE",FACE,{"disambiguationData":[OSD([subQ1,subQ0])]})]}),makeQuery(id+"F14.opExtrude","SWEPT_FACE",FACE,{"disambiguationData":[OSD([sQuery(id+"F13.wireOp",EDGE,"E149.top")])]}),makeQuery(id+"F16.opExtrude","SWEPT_FACE",FACE,{"disambiguationData":[OSD([sQuery(id+"F15.wireOp",EDGE,"E150.top")])]})]});}
            var sketch = newSketch(context, id + "F21", { "sketchPlane" : qUnion([Q0])});
            skLineSegment(sketch, "E157.bottom", {"start": v(0, 6000) * mm, "end": v(10000, 6000) * mm});
            skLineSegment(sketch, "E157.top", {"start": v(0, 0) * mm, "end": v(10000, 0) * mm});
            skLineSegment(sketch, "E157.right", {"start": v(10000, 6000) * mm, "end": v(10000, 0) * mm});
            skPoint(sketch, "E158", {"position": v(0, 3550) * mm});
            skPoint(sketch, "E159", {"position": v(0, 1450) * mm});
            skLineSegment(sketch, "E160.trimOffspring", {"start": v(0, 1450) * mm, "end": v(0, 0) * mm});
            skLineSegment(sketch, "E161", {"start": v(4000, 3500) * mm, "end": v(4000, 6000) * mm});
            skLineSegment(sketch, "E162", {"start": v(4000, 0) * mm, "end": v(4000, 2500) * mm});
            skLineSegment(sketch, "E163", {"start": v(4000, 2500) * mm, "end": v(4550, 2500) * mm});
            skLineSegment(sketch, "E164", {"start": v(4000, 3500) * mm, "end": v(4550, 3500) * mm});
            skLineSegment(sketch, "E165", {"start": v(7500, 3500) * mm, "end": v(7500, 6000) * mm});
            skLineSegment(sketch, "E166", {"start": v(7500, 3500) * mm, "end": v(8050, 3500) * mm});
            skLineSegment(sketch, "E167.bottom", {"start": v(50, 5950) * mm, "end": v(3950, 5950) * mm});
            skLineSegment(sketch, "E167.top", {"start": v(50, 3550) * mm, "end": v(2950, 3550) * mm});
            skLineSegment(sketch, "E167.left", {"start": v(50, 5950) * mm, "end": v(50, 3550) * mm});
            skLineSegment(sketch, "E167.right", {"start": v(3950, 5950) * mm, "end": v(3950, 3550) * mm});
            skLineSegment(sketch, "E168.bottom", {"start": v(4050, 5950) * mm, "end": v(7450, 5950) * mm});
            skLineSegment(sketch, "E168.top", {"start": v(4050, 3550) * mm, "end": v(4550, 3550) * mm});
            skLineSegment(sketch, "E168.left", {"start": v(4050, 5950) * mm, "end": v(4050, 3550) * mm});
            skLineSegment(sketch, "E168.right", {"start": v(7450, 5950) * mm, "end": v(7450, 3550) * mm});
            skLineSegment(sketch, "E169.bottom", {"start": v(7550, 5950) * mm, "end": v(9950, 5950) * mm});
            skLineSegment(sketch, "E169.top", {"start": v(7550, 3550) * mm, "end": v(8050, 3550) * mm});
            skLineSegment(sketch, "E169.left", {"start": v(7550, 5950) * mm, "end": v(7550, 3550) * mm});
            skLineSegment(sketch, "E169.right", {"start": v(9950, 5950) * mm, "end": v(9950, 3550) * mm});
            skLineSegment(sketch, "E170", {"start": v(9950, 3500) * mm, "end": v(9950, 2500) * mm});
            skLineSegment(sketch, "E171.bottom", {"start": v(4050, 2450) * mm, "end": v(4550, 2450) * mm});
            skLineSegment(sketch, "E171.top", {"start": v(4050, 50) * mm, "end": v(9950, 50) * mm});
            skLineSegment(sketch, "E171.left", {"start": v(4050, 2450) * mm, "end": v(4050, 50) * mm});
            skLineSegment(sketch, "E171.right", {"start": v(9950, 2450) * mm, "end": v(9950, 50) * mm});
            skLineSegment(sketch, "E172", {"start": v(0, 1450) * mm, "end": v(0, 1500) * mm});
            skLineSegment(sketch, "E173", {"start": v(0, 1500) * mm, "end": v(50, 1500) * mm});
            skLineSegment(sketch, "E174", {"start": v(50, 1500) * mm, "end": v(50, 0) * mm});
            skLineSegment(sketch, "E175", {"start": v(4000, 50) * mm, "end": v(50, 50) * mm});
            skPoint(sketch, "E176", {"position": v(3450, 3550) * mm});
            skPoint(sketch, "E177", {"position": v(2950, 3550) * mm});
            skPoint(sketch, "E178", {"position": v(3450, 3500) * mm});
            skLineSegment(sketch, "E179", {"start": v(3450, 3550) * mm, "end": v(3450, 3500) * mm});
            skLineSegment(sketch, "E180.trimOffspring", {"start": v(3450, 3550) * mm, "end": v(3950, 3550) * mm});
            skLineSegment(sketch, "E181.trimOffspring", {"start": v(3450, 3500) * mm, "end": v(4000, 3500) * mm});
            skPoint(sketch, "E182", {"position": v(4550, 3550) * mm});
            skPoint(sketch, "E183", {"position": v(5050, 3550) * mm});
            skPoint(sketch, "E184", {"position": v(4550, 3500) * mm});
            skPoint(sketch, "E185", {"position": v(5050, 3500) * mm});
            skLineSegment(sketch, "E186", {"start": v(4550, 3550) * mm, "end": v(4550, 3500) * mm});
            skLineSegment(sketch, "E187", {"start": v(5050, 3550) * mm, "end": v(5050, 3500) * mm});
            skLineSegment(sketch, "E188.trimOffspring", {"start": v(5050, 3550) * mm, "end": v(7450, 3550) * mm});
            skLineSegment(sketch, "E189.trimOffspring", {"start": v(5050, 3500) * mm, "end": v(7500, 3500) * mm});
            skPoint(sketch, "E190", {"position": v(8050, 3550) * mm});
            skPoint(sketch, "E191", {"position": v(4550, 2500) * mm});
            skPoint(sketch, "E192", {"position": v(4550, 2450) * mm});
            skPoint(sketch, "E193", {"position": v(5050, 2500) * mm});
            skPoint(sketch, "E194", {"position": v(5050, 2450) * mm});
            skPoint(sketch, "E195", {"position": v(8550, 3550) * mm});
            skPoint(sketch, "E196", {"position": v(8050, 3500) * mm});
            skPoint(sketch, "E197", {"position": v(8550, 3500) * mm});
            skPoint(sketch, "E198", {"position": v(9450, 2500) * mm});
            skPoint(sketch, "E199", {"position": v(9450, 2450) * mm});
            skPoint(sketch, "E200", {"position": v(8950, 2500) * mm});
            skPoint(sketch, "E201", {"position": v(8950, 2450) * mm});
            skLineSegment(sketch, "E202", {"start": v(8950, 2500) * mm, "end": v(8950, 2450) * mm});
            skLineSegment(sketch, "E203", {"start": v(9450, 2500) * mm, "end": v(9450, 2450) * mm});
            skLineSegment(sketch, "E204", {"start": v(8550, 3550) * mm, "end": v(8550, 3500) * mm});
            skLineSegment(sketch, "E205", {"start": v(8050, 3550) * mm, "end": v(8050, 3500) * mm});
            skLineSegment(sketch, "E206", {"start": v(4550, 2500) * mm, "end": v(4550, 2450) * mm});
            skLineSegment(sketch, "E207", {"start": v(5050, 2500) * mm, "end": v(5050, 2450) * mm});
            skLineSegment(sketch, "E208.trimOffspring", {"start": v(5050, 2500) * mm, "end": v(8950, 2500) * mm});
            skLineSegment(sketch, "E209.trimOffspring", {"start": v(5050, 2450) * mm, "end": v(8950, 2450) * mm});
            skLineSegment(sketch, "E210.trimOffspring", {"start": v(8550, 3550) * mm, "end": v(9950, 3550) * mm});
            skLineSegment(sketch, "E211.trimOffspring", {"start": v(8550, 3500) * mm, "end": v(10000, 3500) * mm});
            skLineSegment(sketch, "E212.trimOffspring", {"start": v(9450, 2500) * mm, "end": v(10000, 2500) * mm});
            skLineSegment(sketch, "E213.trimOffspring", {"start": v(9450, 2450) * mm, "end": v(9950, 2450) * mm});
            skLineSegment(sketch, "E214", {"start": v(0, 6000) * mm, "end": v(0, 3550) * mm});
            skLineSegment(sketch, "E215", {"start": v(0, 3500) * mm, "end": v(0, 3550) * mm});
            skLineSegment(sketch, "E216", {"start": v(0, 3500) * mm, "end": v(2950, 3500) * mm});
            skLineSegment(sketch, "E217", {"start": v(2950, 3500) * mm, "end": v(2950, 3550) * mm});
            skSolve(sketch);
        }
        {
            var Q0;
            Q0=qSketchRegion(id+"F21",true);
            extrude(context, id + "F22", {"entities" : qUnion([Q0]), "operationType" : NewBodyOperationType.ADD, "depth" : 2500 * mm, "offsetDistance" : 25 * mm});
        }
        {
            var Q0;
            Q0=makeQuery(id+"F22.opExtrude","CAP_FACE",FACE,{"disambiguationData":[OSD([sQuery(id+"F21.wireOp",EDGE,"E157.bottom"),sQuery(id+"F21.wireOp",EDGE,"E157.top"),sQuery(id+"F21.wireOp",EDGE,"E157.right"),sQuery(id+"F21.wireOp",EDGE,"E160.trimOffspring"),sQuery(id+"F21.wireOp",EDGE,"E162"),sQuery(id+"F21.wireOp",EDGE,"E163"),sQuery(id+"F21.wireOp",EDGE,"E164"),sQuery(id+"F21.wireOp",EDGE,"E166"),sQuery(id+"F21.wireOp",EDGE,"E167.bottom"),sQuery(id+"F21.wireOp",EDGE,"E167.top"),sQuery(id+"F21.wireOp",EDGE,"E167.left"),sQuery(id+"F21.wireOp",EDGE,"E167.right"),sQuery(id+"F21.wireOp",EDGE,"E168.bottom"),sQuery(id+"F21.wireOp",EDGE,"E168.top"),sQuery(id+"F21.wireOp",EDGE,"E168.left"),sQuery(id+"F21.wireOp",EDGE,"E168.right"),sQuery(id+"F21.wireOp",EDGE,"E169.bottom"),sQuery(id+"F21.wireOp",EDGE,"E169.top"),sQuery(id+"F21.wireOp",EDGE,"E169.left"),sQuery(id+"F21.wireOp",EDGE,"E169.right"),sQuery(id+"F21.wireOp",EDGE,"E170"),sQuery(id+"F21.wireOp",EDGE,"E171.bottom"),sQuery(id+"F21.wireOp",EDGE,"E171.top"),sQuery(id+"F21.wireOp",EDGE,"E171.left"),sQuery(id+"F21.wireOp",EDGE,"E171.right"),sQuery(id+"F21.wireOp",EDGE,"E172"),sQuery(id+"F21.wireOp",EDGE,"E173"),sQuery(id+"F21.wireOp",EDGE,"E174"),sQuery(id+"F21.wireOp",EDGE,"E175"),sQuery(id+"F21.wireOp",EDGE,"E179"),sQuery(id+"F21.wireOp",EDGE,"E180.trimOffspring"),sQuery(id+"F21.wireOp",EDGE,"E181.trimOffspring"),sQuery(id+"F21.wireOp",EDGE,"E186"),sQuery(id+"F21.wireOp",EDGE,"E187"),sQuery(id+"F21.wireOp",EDGE,"E188.trimOffspring"),sQuery(id+"F21.wireOp",EDGE,"E189.trimOffspring"),sQuery(id+"F21.wireOp",EDGE,"E203"),sQuery(id+"F21.wireOp",EDGE,"E204"),sQuery(id+"F21.wireOp",EDGE,"E205"),sQuery(id+"F21.wireOp",EDGE,"E206"),sQuery(id+"F21.wireOp",EDGE,"E210.trimOffspring"),sQuery(id+"F21.wireOp",EDGE,"E211.trimOffspring"),sQuery(id+"F21.wireOp",EDGE,"E212.trimOffspring"),sQuery(id+"F21.wireOp",EDGE,"E213.trimOffspring"),sQuery(id+"F21.wireOp",EDGE,"E214"),sQuery(id+"F21.wireOp",EDGE,"E215"),sQuery(id+"F21.wireOp",EDGE,"E216"),sQuery(id+"F21.wireOp",EDGE,"E217")])],"isStart":false});
            var sketch = newSketch(context, id + "F23", { "sketchPlane" : qUnion([Q0])});
            skLineSegment(sketch, "E218.bottom", {"start": v(0, 6000) * mm, "end": v(10000, 6000) * mm});
            skLineSegment(sketch, "E218.top", {"start": v(0, 0) * mm, "end": v(10000, 0) * mm});
            skLineSegment(sketch, "E218.right", {"start": v(10000, 6000) * mm, "end": v(10000, 0) * mm});
            skPoint(sketch, "E219", {"position": v(0, 3550) * mm});
            skPoint(sketch, "E220", {"position": v(0, 1450) * mm});
            skLineSegment(sketch, "E221.trimOffspring", {"start": v(0, 1450) * mm, "end": v(0, 0) * mm});
            skLineSegment(sketch, "E222", {"start": v(4000, 3500) * mm, "end": v(4000, 6000) * mm});
            skLineSegment(sketch, "E223", {"start": v(4000, 0) * mm, "end": v(4000, 2500) * mm});
            skLineSegment(sketch, "E224", {"start": v(4000, 2500) * mm, "end": v(4550, 2500) * mm});
            skLineSegment(sketch, "E225", {"start": v(4000, 3500) * mm, "end": v(4550, 3500) * mm});
            skLineSegment(sketch, "E226", {"start": v(7500, 3500) * mm, "end": v(7500, 6000) * mm});
            skLineSegment(sketch, "E227", {"start": v(7500, 3500) * mm, "end": v(8050, 3500) * mm});
            skLineSegment(sketch, "E228.bottom", {"start": v(50, 5950) * mm, "end": v(3950, 5950) * mm});
            skLineSegment(sketch, "E228.top", {"start": v(50, 3550) * mm, "end": v(2950, 3550) * mm});
            skLineSegment(sketch, "E228.left", {"start": v(50, 5950) * mm, "end": v(50, 3550) * mm});
            skLineSegment(sketch, "E228.right", {"start": v(3950, 5950) * mm, "end": v(3950, 3550) * mm});
            skLineSegment(sketch, "E229.bottom", {"start": v(4050, 5950) * mm, "end": v(7450, 5950) * mm});
            skLineSegment(sketch, "E229.top", {"start": v(4050, 3550) * mm, "end": v(4550, 3550) * mm});
            skLineSegment(sketch, "E229.left", {"start": v(4050, 5950) * mm, "end": v(4050, 3550) * mm});
            skLineSegment(sketch, "E229.right", {"start": v(7450, 5950) * mm, "end": v(7450, 3550) * mm});
            skLineSegment(sketch, "E230.bottom", {"start": v(7550, 5950) * mm, "end": v(9950, 5950) * mm});
            skLineSegment(sketch, "E230.top", {"start": v(7550, 3550) * mm, "end": v(8050, 3550) * mm});
            skLineSegment(sketch, "E230.left", {"start": v(7550, 5950) * mm, "end": v(7550, 3550) * mm});
            skLineSegment(sketch, "E230.right", {"start": v(9950, 5950) * mm, "end": v(9950, 3550) * mm});
            skLineSegment(sketch, "E231", {"start": v(9950, 3500) * mm, "end": v(9950, 2500) * mm});
            skLineSegment(sketch, "E232.bottom", {"start": v(4050, 2450) * mm, "end": v(4550, 2450) * mm});
            skLineSegment(sketch, "E232.top", {"start": v(4050, 50) * mm, "end": v(9950, 50) * mm});
            skLineSegment(sketch, "E232.left", {"start": v(4050, 2450) * mm, "end": v(4050, 50) * mm});
            skLineSegment(sketch, "E232.right", {"start": v(9950, 2450) * mm, "end": v(9950, 50) * mm});
            skLineSegment(sketch, "E233", {"start": v(0, 1450) * mm, "end": v(0, 1500) * mm});
            skLineSegment(sketch, "E234", {"start": v(0, 1500) * mm, "end": v(50, 1500) * mm});
            skLineSegment(sketch, "E235", {"start": v(50, 1500) * mm, "end": v(50, 0) * mm});
            skLineSegment(sketch, "E236", {"start": v(4000, 50) * mm, "end": v(50, 50) * mm});
            skPoint(sketch, "E237", {"position": v(3450, 3550) * mm});
            skPoint(sketch, "E238", {"position": v(2950, 3550) * mm});
            skPoint(sketch, "E239", {"position": v(3450, 3500) * mm});
            skLineSegment(sketch, "E240", {"start": v(3450, 3550) * mm, "end": v(3450, 3500) * mm});
            skLineSegment(sketch, "E241.trimOffspring", {"start": v(3450, 3550) * mm, "end": v(3950, 3550) * mm});
            skLineSegment(sketch, "E242.trimOffspring", {"start": v(3450, 3500) * mm, "end": v(4000, 3500) * mm});
            skPoint(sketch, "E243", {"position": v(4550, 3550) * mm});
            skPoint(sketch, "E244", {"position": v(5050, 3550) * mm});
            skPoint(sketch, "E245", {"position": v(4550, 3500) * mm});
            skPoint(sketch, "E246", {"position": v(5050, 3500) * mm});
            skLineSegment(sketch, "E247", {"start": v(4550, 3550) * mm, "end": v(4550, 3500) * mm});
            skLineSegment(sketch, "E248", {"start": v(5050, 3550) * mm, "end": v(5050, 3500) * mm});
            skLineSegment(sketch, "E249.trimOffspring", {"start": v(5050, 3550) * mm, "end": v(7450, 3550) * mm});
            skLineSegment(sketch, "E250.trimOffspring", {"start": v(5050, 3500) * mm, "end": v(7500, 3500) * mm});
            skPoint(sketch, "E251", {"position": v(8050, 3550) * mm});
            skPoint(sketch, "E252", {"position": v(4550, 2500) * mm});
            skPoint(sketch, "E253", {"position": v(4550, 2450) * mm});
            skPoint(sketch, "E254", {"position": v(5050, 2500) * mm});
            skPoint(sketch, "E255", {"position": v(5050, 2450) * mm});
            skPoint(sketch, "E256", {"position": v(8550, 3550) * mm});
            skPoint(sketch, "E257", {"position": v(8050, 3500) * mm});
            skPoint(sketch, "E258", {"position": v(8550, 3500) * mm});
            skPoint(sketch, "E259", {"position": v(9450, 2500) * mm});
            skPoint(sketch, "E260", {"position": v(9450, 2450) * mm});
            skPoint(sketch, "E261", {"position": v(8950, 2500) * mm});
            skPoint(sketch, "E262", {"position": v(8950, 2450) * mm});
            skLineSegment(sketch, "E263", {"start": v(8950, 2500) * mm, "end": v(8950, 2450) * mm});
            skLineSegment(sketch, "E264", {"start": v(9450, 2500) * mm, "end": v(9450, 2450) * mm});
            skLineSegment(sketch, "E265", {"start": v(8550, 3550) * mm, "end": v(8550, 3500) * mm});
            skLineSegment(sketch, "E266", {"start": v(8050, 3550) * mm, "end": v(8050, 3500) * mm});
            skLineSegment(sketch, "E267", {"start": v(4550, 2500) * mm, "end": v(4550, 2450) * mm});
            skLineSegment(sketch, "E268", {"start": v(5050, 2500) * mm, "end": v(5050, 2450) * mm});
            skLineSegment(sketch, "E269.trimOffspring", {"start": v(5050, 2500) * mm, "end": v(8950, 2500) * mm});
            skLineSegment(sketch, "E270.trimOffspring", {"start": v(5050, 2450) * mm, "end": v(8950, 2450) * mm});
            skLineSegment(sketch, "E271.trimOffspring", {"start": v(8550, 3550) * mm, "end": v(9950, 3550) * mm});
            skLineSegment(sketch, "E272.trimOffspring", {"start": v(8550, 3500) * mm, "end": v(10000, 3500) * mm});
            skLineSegment(sketch, "E273.trimOffspring", {"start": v(9450, 2500) * mm, "end": v(10000, 2500) * mm});
            skLineSegment(sketch, "E274.trimOffspring", {"start": v(9450, 2450) * mm, "end": v(9950, 2450) * mm});
            skLineSegment(sketch, "E275", {"start": v(0, 6000) * mm, "end": v(0, 3550) * mm});
            skLineSegment(sketch, "E276", {"start": v(0, 3500) * mm, "end": v(0, 3550) * mm});
            skLineSegment(sketch, "E277", {"start": v(0, 3500) * mm, "end": v(2950, 3500) * mm});
            skLineSegment(sketch, "E278", {"start": v(2950, 3500) * mm, "end": v(2950, 3550) * mm});
            skLineSegment(sketch, "E279", {"start": v(2950, 3550) * mm, "end": v(3450, 3550) * mm});
            skLineSegment(sketch, "E280", {"start": v(3450, 3500) * mm, "end": v(2950, 3500) * mm});
            skLineSegment(sketch, "E281", {"start": v(4550, 3550) * mm, "end": v(5050, 3550) * mm});
            skLineSegment(sketch, "E282", {"start": v(5050, 3500) * mm, "end": v(4550, 3500) * mm});
            skLineSegment(sketch, "E283", {"start": v(4550, 2500) * mm, "end": v(5050, 2500) * mm});
            skLineSegment(sketch, "E284", {"start": v(4550, 2450) * mm, "end": v(5050, 2450) * mm});
            skLineSegment(sketch, "E285", {"start": v(8050, 3550) * mm, "end": v(8550, 3550) * mm});
            skLineSegment(sketch, "E286", {"start": v(8550, 3500) * mm, "end": v(8050, 3500) * mm});
            skLineSegment(sketch, "E287", {"start": v(8950, 2500) * mm, "end": v(9450, 2500) * mm});
            skLineSegment(sketch, "E288", {"start": v(9450, 2450) * mm, "end": v(8950, 2450) * mm});
            skSolve(sketch);
        }
        {
            var Q0;
            Q0=qSketchRegion(id+"F23",true);
            extrude(context, id + "F24", {"entities" : qUnion([Q0]), "operationType" : NewBodyOperationType.ADD, "oppositeDirection" : true, "depth" : 750 * mm, "offsetDistance" : 25 * mm});
        }
        {
            var Q0;
            Q0=makeQuery(id+"F24.boolean.opBoolean","MERGE",FACE,{"derivedFrom":[makeQuery(id+"F22.opExtrude","CAP_FACE",FACE,{"disambiguationData":[OSD([sQuery(id+"F21.wireOp",EDGE,"E157.bottom"),sQuery(id+"F21.wireOp",EDGE,"E157.top"),sQuery(id+"F21.wireOp",EDGE,"E157.right"),sQuery(id+"F21.wireOp",EDGE,"E160.trimOffspring"),sQuery(id+"F21.wireOp",EDGE,"E162"),sQuery(id+"F21.wireOp",EDGE,"E163"),sQuery(id+"F21.wireOp",EDGE,"E164"),sQuery(id+"F21.wireOp",EDGE,"E166"),sQuery(id+"F21.wireOp",EDGE,"E167.bottom"),sQuery(id+"F21.wireOp",EDGE,"E167.top"),sQuery(id+"F21.wireOp",EDGE,"E167.left"),sQuery(id+"F21.wireOp",EDGE,"E167.right"),sQuery(id+"F21.wireOp",EDGE,"E168.bottom"),sQuery(id+"F21.wireOp",EDGE,"E168.top"),sQuery(id+"F21.wireOp",EDGE,"E168.left"),sQuery(id+"F21.wireOp",EDGE,"E168.right"),sQuery(id+"F21.wireOp",EDGE,"E169.bottom"),sQuery(id+"F21.wireOp",EDGE,"E169.top"),sQuery(id+"F21.wireOp",EDGE,"E169.left"),sQuery(id+"F21.wireOp",EDGE,"E169.right"),sQuery(id+"F21.wireOp",EDGE,"E170"),sQuery(id+"F21.wireOp",EDGE,"E171.bottom"),sQuery(id+"F21.wireOp",EDGE,"E171.top"),sQuery(id+"F21.wireOp",EDGE,"E171.left"),sQuery(id+"F21.wireOp",EDGE,"E171.right"),sQuery(id+"F21.wireOp",EDGE,"E172"),sQuery(id+"F21.wireOp",EDGE,"E173"),sQuery(id+"F21.wireOp",EDGE,"E174"),sQuery(id+"F21.wireOp",EDGE,"E175"),sQuery(id+"F21.wireOp",EDGE,"E179"),sQuery(id+"F21.wireOp",EDGE,"E180.trimOffspring"),sQuery(id+"F21.wireOp",EDGE,"E181.trimOffspring"),sQuery(id+"F21.wireOp",EDGE,"E186"),sQuery(id+"F21.wireOp",EDGE,"E187"),sQuery(id+"F21.wireOp",EDGE,"E188.trimOffspring"),sQuery(id+"F21.wireOp",EDGE,"E189.trimOffspring"),sQuery(id+"F21.wireOp",EDGE,"E203"),sQuery(id+"F21.wireOp",EDGE,"E204"),sQuery(id+"F21.wireOp",EDGE,"E205"),sQuery(id+"F21.wireOp",EDGE,"E206"),sQuery(id+"F21.wireOp",EDGE,"E210.trimOffspring"),sQuery(id+"F21.wireOp",EDGE,"E211.trimOffspring"),sQuery(id+"F21.wireOp",EDGE,"E212.trimOffspring"),sQuery(id+"F21.wireOp",EDGE,"E213.trimOffspring"),sQuery(id+"F21.wireOp",EDGE,"E214"),sQuery(id+"F21.wireOp",EDGE,"E215"),sQuery(id+"F21.wireOp",EDGE,"E216"),sQuery(id+"F21.wireOp",EDGE,"E217")])],"isStart":false}),makeQuery(id+"F22.opExtrude","CAP_FACE",FACE,{"disambiguationData":[OSD([sQuery(id+"F21.wireOp",EDGE,"E202"),sQuery(id+"F21.wireOp",EDGE,"E207"),sQuery(id+"F21.wireOp",EDGE,"E208.trimOffspring"),sQuery(id+"F21.wireOp",EDGE,"E209.trimOffspring")])],"isStart":false}),makeQuery(id+"F24.opExtrude","CAP_FACE",FACE,{"disambiguationData":[OSD([sQuery(id+"F23.wireOp",EDGE,"E218.bottom"),sQuery(id+"F23.wireOp",EDGE,"E218.top"),sQuery(id+"F23.wireOp",EDGE,"E218.right"),sQuery(id+"F23.wireOp",EDGE,"E221.trimOffspring"),sQuery(id+"F23.wireOp",EDGE,"E223"),sQuery(id+"F23.wireOp",EDGE,"E224"),sQuery(id+"F23.wireOp",EDGE,"E225"),sQuery(id+"F23.wireOp",EDGE,"E227"),sQuery(id+"F23.wireOp",EDGE,"E228.bottom"),sQuery(id+"F23.wireOp",EDGE,"E228.top"),sQuery(id+"F23.wireOp",EDGE,"E228.left"),sQuery(id+"F23.wireOp",EDGE,"E228.right"),sQuery(id+"F23.wireOp",EDGE,"E229.bottom"),sQuery(id+"F23.wireOp",EDGE,"E229.top"),sQuery(id+"F23.wireOp",EDGE,"E229.left"),sQuery(id+"F23.wireOp",EDGE,"E229.right"),sQuery(id+"F23.wireOp",EDGE,"E230.bottom"),sQuery(id+"F23.wireOp",EDGE,"E230.top"),sQuery(id+"F23.wireOp",EDGE,"E230.left"),sQuery(id+"F23.wireOp",EDGE,"E230.right"),sQuery(id+"F23.wireOp",EDGE,"E231"),sQuery(id+"F23.wireOp",EDGE,"E232.bottom"),sQuery(id+"F23.wireOp",EDGE,"E232.top"),sQuery(id+"F23.wireOp",EDGE,"E232.left"),sQuery(id+"F23.wireOp",EDGE,"E232.right"),sQuery(id+"F23.wireOp",EDGE,"E233"),sQuery(id+"F23.wireOp",EDGE,"E234"),sQuery(id+"F23.wireOp",EDGE,"E235"),sQuery(id+"F23.wireOp",EDGE,"E236"),sQuery(id+"F23.wireOp",EDGE,"E241.trimOffspring"),sQuery(id+"F23.wireOp",EDGE,"E242.trimOffspring"),sQuery(id+"F23.wireOp",EDGE,"E249.trimOffspring"),sQuery(id+"F23.wireOp",EDGE,"E250.trimOffspring"),sQuery(id+"F23.wireOp",EDGE,"E269.trimOffspring"),sQuery(id+"F23.wireOp",EDGE,"E270.trimOffspring"),sQuery(id+"F23.wireOp",EDGE,"E271.trimOffspring"),sQuery(id+"F23.wireOp",EDGE,"E272.trimOffspring"),sQuery(id+"F23.wireOp",EDGE,"E273.trimOffspring"),sQuery(id+"F23.wireOp",EDGE,"E274.trimOffspring"),sQuery(id+"F23.wireOp",EDGE,"E275"),sQuery(id+"F23.wireOp",EDGE,"E276"),sQuery(id+"F23.wireOp",EDGE,"E277"),sQuery(id+"F23.wireOp",EDGE,"E279"),sQuery(id+"F23.wireOp",EDGE,"E280"),sQuery(id+"F23.wireOp",EDGE,"E281"),sQuery(id+"F23.wireOp",EDGE,"E282"),sQuery(id+"F23.wireOp",EDGE,"E283"),sQuery(id+"F23.wireOp",EDGE,"E284"),sQuery(id+"F23.wireOp",EDGE,"E285"),sQuery(id+"F23.wireOp",EDGE,"E286"),sQuery(id+"F23.wireOp",EDGE,"E287"),sQuery(id+"F23.wireOp",EDGE,"E288")])],"isStart":true})]});
            var sketch = newSketch(context, id + "F25", { "sketchPlane" : qUnion([Q0])});
            skLineSegment(sketch, "E289.bottom", {"start": v(0, 6000) * mm, "end": v(10000, 6000) * mm});
            skLineSegment(sketch, "E289.top", {"start": v(0, 0) * mm, "end": v(10000, 0) * mm});
            skLineSegment(sketch, "E289.left", {"start": v(0, 6000) * mm, "end": v(0, 0) * mm});
            skLineSegment(sketch, "E289.right", {"start": v(10000, 6000) * mm, "end": v(10000, 0) * mm});
            skSolve(sketch);
        }
        {
            var Q0;
            Q0=qSketchRegion(id+"F25",true);
            extrude(context, id + "F26", {"entities" : qUnion([Q0]), "operationType" : NewBodyOperationType.ADD, "depth" : 25 * mm, "offsetDistance" : 25 * mm});
        }
        {
            var Q0;
            Q0=makeQuery(id+"F26.boolean.opBoolean","MERGE",FACE,{"derivedFrom":[makeQuery(id+"F22.boolean.opBoolean","MERGE",FACE,{"derivedFrom":[makeQuery(id+"F12.opExtrude","CAP_FACE",FACE,{"disambiguationData":[OSD([sQuery(id+"F0.wireOp",EDGE,"E0.top"),sQuery(id+"F1.wireOp",EDGE,"E1.top"),sQuery(id+"F5.wireOp",EDGE,"E53.top"),sQuery(id+"F7.wireOp",EDGE,"E54.top"),sQuery(id+"F7.wireOp",EDGE,"E116")])],"isStart":false}),makeQuery(id+"F22.opExtrude","SWEPT_FACE",FACE,{"disambiguationData":[OSD([sQuery(id+"F21.wireOp",EDGE,"E157.bottom")])]})]}),makeQuery(id+"F26.opExtrude","SWEPT_FACE",FACE,{"disambiguationData":[OSD([sQuery(id+"F25.wireOp",EDGE,"E289.bottom")])]})]});
            var sketch = newSketch(context, id + "F27", { "sketchPlane" : qUnion([Q0])});
            skLineSegment(sketch, "E290.bottom", {"start": v(-3850, 1500) * mm, "end": v(-2850, 1500) * mm});
            skLineSegment(sketch, "E290.top", {"start": v(-3850, 750) * mm, "end": v(-2850, 750) * mm});
            skLineSegment(sketch, "E290.left", {"start": v(-3850, 1500) * mm, "end": v(-3850, 750) * mm});
            skLineSegment(sketch, "E290.right", {"start": v(-2850, 1500) * mm, "end": v(-2850, 750) * mm});
            skLineSegment(sketch, "E291.bottom", {"start": v(-1750, 1500) * mm, "end": v(-750, 1500) * mm});
            skLineSegment(sketch, "E291.top", {"start": v(-1750, 750) * mm, "end": v(-750, 750) * mm});
            skLineSegment(sketch, "E291.left", {"start": v(-1750, 1500) * mm, "end": v(-1750, 750) * mm});
            skLineSegment(sketch, "E291.right", {"start": v(-750, 1500) * mm, "end": v(-750, 750) * mm});
            skLineSegment(sketch, "E292.bottom", {"start": v(-3850, 3792.4) * mm, "end": v(-2850, 3792.4) * mm});
            skLineSegment(sketch, "E292.top", {"start": v(-3850, 4542.4) * mm, "end": v(-2850, 4542.4) * mm});
            skLineSegment(sketch, "E292.left", {"start": v(-3850, 3792.4) * mm, "end": v(-3850, 4542.4) * mm});
            skLineSegment(sketch, "E292.right", {"start": v(-2850, 3792.4) * mm, "end": v(-2850, 4542.4) * mm});
            skLineSegment(sketch, "E293.bottom", {"start": v(-1750, 3792.4) * mm, "end": v(-750, 3792.4) * mm});
            skLineSegment(sketch, "E293.top", {"start": v(-1750, 4542.4) * mm, "end": v(-750, 4542.4) * mm});
            skLineSegment(sketch, "E293.left", {"start": v(-1750, 3792.4) * mm, "end": v(-1750, 4542.4) * mm});
            skLineSegment(sketch, "E293.right", {"start": v(-750, 3792.4) * mm, "end": v(-750, 4542.4) * mm});
            skLineSegment(sketch, "E294.bottom", {"start": v(-9250, 1500) * mm, "end": v(-8250, 1500) * mm});
            skLineSegment(sketch, "E294.top", {"start": v(-9250, 750) * mm, "end": v(-8250, 750) * mm});
            skLineSegment(sketch, "E294.left", {"start": v(-9250, 1500) * mm, "end": v(-9250, 750) * mm});
            skLineSegment(sketch, "E294.right", {"start": v(-8250, 1500) * mm, "end": v(-8250, 750) * mm});
            skLineSegment(sketch, "E295.bottom", {"start": v(-7150, 1500) * mm, "end": v(-6150, 1500) * mm});
            skLineSegment(sketch, "E295.top", {"start": v(-7150, 750) * mm, "end": v(-6150, 750) * mm});
            skLineSegment(sketch, "E295.left", {"start": v(-7150, 1500) * mm, "end": v(-7150, 750) * mm});
            skLineSegment(sketch, "E295.right", {"start": v(-6150, 1500) * mm, "end": v(-6150, 750) * mm});
            skLineSegment(sketch, "E296.bottom", {"start": v(-9250, 3792.4) * mm, "end": v(-8250, 3792.4) * mm});
            skLineSegment(sketch, "E296.top", {"start": v(-9250, 4542.4) * mm, "end": v(-8250, 4542.4) * mm});
            skLineSegment(sketch, "E296.left", {"start": v(-9250, 3792.4) * mm, "end": v(-9250, 4542.4) * mm});
            skLineSegment(sketch, "E296.right", {"start": v(-8250, 3792.4) * mm, "end": v(-8250, 4542.4) * mm});
            skLineSegment(sketch, "E297.bottom", {"start": v(-7150, 3792.4) * mm, "end": v(-6150, 3792.4) * mm});
            skLineSegment(sketch, "E297.top", {"start": v(-7150, 4542.4) * mm, "end": v(-6150, 4542.4) * mm});
            skLineSegment(sketch, "E297.left", {"start": v(-7150, 3792.4) * mm, "end": v(-7150, 4542.4) * mm});
            skLineSegment(sketch, "E297.right", {"start": v(-6150, 3792.4) * mm, "end": v(-6150, 4542.4) * mm});
            skSolve(sketch);
        }
        {
            var Q0;
            Q0 = qSketchRegion(id + "F27", true);
            extrude(context, id + "F28", {"entities" : qUnion([Q0]), "operationType" : NewBodyOperationType.REMOVE, "oppositeDirection" : true, "depth" : 50 * mm, "offsetDistance" : 25 * mm});
        }
        {
            var Q0;
            {var subQ0=makeQuery(id+"F6.boolean.opBoolean","MERGE",FACE,{"derivedFrom":[makeQuery(id+"F3.boolean.opBoolean","MERGE",FACE,{"derivedFrom":[makeQuery(id+"F2.opExtrude","SWEPT_FACE",FACE,{"disambiguationData":[OSD([sQuery(id+"F0.wireOp",EDGE,"E0.bottom")])]}),makeQuery(id+"F3.opExtrude","SWEPT_FACE",FACE,{"disambiguationData":[OSD([sQuery(id+"F1.wireOp",EDGE,"E1.bottom")])]})]}),makeQuery(id+"F6.opExtrude","SWEPT_FACE",FACE,{"disambiguationData":[OSD([sQuery(id+"F5.wireOp",EDGE,"E53.bottom")])]})]});Q0=makeQuery(id+"F26.boolean.opBoolean","MERGE",FACE,{"derivedFrom":[makeQuery(id+"F22.boolean.opBoolean","MERGE",FACE,{"derivedFrom":[makeQuery(id+"F9.boolean.opBoolean","MERGE",FACE,{"derivedFrom":[subQ0,makeQuery(id+"F9.opPattern","COPY",FACE,{"derivedFrom":subQ0,"instanceName":"1"})]}),makeQuery(id+"F22.opExtrude","SWEPT_FACE",FACE,{"disambiguationData":[OSD([sQuery(id+"F21.wireOp",EDGE,"E157.top")])]})]}),makeQuery(id+"F26.opExtrude","SWEPT_FACE",FACE,{"disambiguationData":[OSD([sQuery(id+"F25.wireOp",EDGE,"E289.top")])]})]});}
            var sketch = newSketch(context, id + "F29", { "sketchPlane" : qUnion([Q0])});
            skLineSegment(sketch, "E298.bottom", {"start": v(6150, 1475) * mm, "end": v(7150, 1475) * mm});
            skLineSegment(sketch, "E298.top", {"start": v(6150, 725) * mm, "end": v(7150, 725) * mm});
            skLineSegment(sketch, "E298.left", {"start": v(6150, 1475) * mm, "end": v(6150, 725) * mm});
            skLineSegment(sketch, "E298.right", {"start": v(7150, 1475) * mm, "end": v(7150, 725) * mm});
            skLineSegment(sketch, "E299.bottom", {"start": v(8250, 1475) * mm, "end": v(9250, 1475) * mm});
            skLineSegment(sketch, "E299.top", {"start": v(8250, 725) * mm, "end": v(9250, 725) * mm});
            skLineSegment(sketch, "E299.left", {"start": v(8250, 1475) * mm, "end": v(8250, 725) * mm});
            skLineSegment(sketch, "E299.right", {"start": v(9250, 1475) * mm, "end": v(9250, 725) * mm});
            skLineSegment(sketch, "E300.bottom", {"start": v(6150, 3762.4) * mm, "end": v(7150, 3762.4) * mm});
            skLineSegment(sketch, "E300.top", {"start": v(6150, 4512.4) * mm, "end": v(7150, 4512.4) * mm});
            skLineSegment(sketch, "E300.left", {"start": v(6150, 3762.4) * mm, "end": v(6150, 4512.4) * mm});
            skLineSegment(sketch, "E300.right", {"start": v(7150, 3762.4) * mm, "end": v(7150, 4512.4) * mm});
            skLineSegment(sketch, "E301.bottom", {"start": v(8250, 3762.4) * mm, "end": v(9250, 3762.4) * mm});
            skLineSegment(sketch, "E301.top", {"start": v(8250, 4512.4) * mm, "end": v(9250, 4512.4) * mm});
            skLineSegment(sketch, "E301.left", {"start": v(8250, 3762.4) * mm, "end": v(8250, 4512.4) * mm});
            skLineSegment(sketch, "E301.right", {"start": v(9250, 3762.4) * mm, "end": v(9250, 4512.4) * mm});
            skLineSegment(sketch, "E302.bottom", {"start": v(750, 1470) * mm, "end": v(1750, 1470) * mm});
            skLineSegment(sketch, "E302.top", {"start": v(750, 720) * mm, "end": v(1750, 720) * mm});
            skLineSegment(sketch, "E302.left", {"start": v(750, 1470) * mm, "end": v(750, 720) * mm});
            skLineSegment(sketch, "E302.right", {"start": v(1750, 1470) * mm, "end": v(1750, 720) * mm});
            skLineSegment(sketch, "E303.bottom", {"start": v(2850, 1470) * mm, "end": v(3850, 1470) * mm});
            skLineSegment(sketch, "E303.top", {"start": v(2850, 720) * mm, "end": v(3850, 720) * mm});
            skLineSegment(sketch, "E303.left", {"start": v(2850, 1470) * mm, "end": v(2850, 720) * mm});
            skLineSegment(sketch, "E303.right", {"start": v(3850, 1470) * mm, "end": v(3850, 720) * mm});
            skLineSegment(sketch, "E304.bottom", {"start": v(750, 3762.4) * mm, "end": v(1750, 3762.4) * mm});
            skLineSegment(sketch, "E304.top", {"start": v(750, 4512.4) * mm, "end": v(1750, 4512.4) * mm});
            skLineSegment(sketch, "E304.left", {"start": v(750, 3762.4) * mm, "end": v(750, 4512.4) * mm});
            skLineSegment(sketch, "E304.right", {"start": v(1750, 3762.4) * mm, "end": v(1750, 4512.4) * mm});
            skLineSegment(sketch, "E305.bottom", {"start": v(2850, 3762.4) * mm, "end": v(3850, 3762.4) * mm});
            skLineSegment(sketch, "E305.top", {"start": v(2850, 4512.4) * mm, "end": v(3850, 4512.4) * mm});
            skLineSegment(sketch, "E305.left", {"start": v(2850, 3762.4) * mm, "end": v(2850, 4512.4) * mm});
            skLineSegment(sketch, "E305.right", {"start": v(3850, 3762.4) * mm, "end": v(3850, 4512.4) * mm});
            skSolve(sketch);
        }
        {
            var Q0;
            Q0 = qSketchRegion(id + "F29", true);
            extrude(context, id + "F30", {"entities" : qUnion([Q0]), "operationType" : NewBodyOperationType.REMOVE, "oppositeDirection" : true, "depth" : 50 * mm, "offsetDistance" : 25 * mm});
        }
        {
            var Q0;
            Q0=makeQuery(id+"F26.boolean.opBoolean","MERGE",FACE,{"derivedFrom":[makeQuery(id+"F22.boolean.opBoolean","MERGE",FACE,{"derivedFrom":[makeQuery(id+"F9.boolean.opBoolean","MERGE",FACE,{"derivedFrom":[makeQuery(id+"F2.opExtrude","SWEPT_FACE",FACE,{"disambiguationData":[OSD([sQuery(id+"F0.wireOp",EDGE,"E0.right")])]}),makeQuery(id+"F6.opExtrude","SWEPT_FACE",FACE,{"disambiguationData":[OSD([sQuery(id+"F5.wireOp",EDGE,"E53.right")])]}),makeQuery(id+"F9.opPattern","COPY",FACE,{"derivedFrom":makeQuery(id+"F8.boolean.opBoolean","MERGE",FACE,{"derivedFrom":[makeQuery(id+"F6.boolean.opBoolean","MERGE",FACE,{"derivedFrom":[makeQuery(id+"F3.boolean.opBoolean","MERGE",FACE,{"derivedFrom":[makeQuery(id+"F2.opExtrude","SWEPT_FACE",FACE,{"disambiguationData":[OSD([sQuery(id+"F0.wireOp",EDGE,"E0.left")])]}),makeQuery(id+"F3.opExtrude","SWEPT_FACE",FACE,{"disambiguationData":[OSD([sQuery(id+"F1.wireOp",EDGE,"E1.left")])]}),makeQuery(id+"F3.opExtrude","SWEPT_FACE",FACE,{"disambiguationData":[OSD([sQuery(id+"F1.wireOp",EDGE,"E22.trimOffspring")])]})]}),makeQuery(id+"F6.opExtrude","SWEPT_FACE",FACE,{"disambiguationData":[OSD([sQuery(id+"F5.wireOp",EDGE,"E53.left")])]})]}),makeQuery(id+"F8.opExtrude","SWEPT_FACE",FACE,{"disambiguationData":[OSD([sQuery(id+"F7.wireOp",EDGE,"E54.left"),sQuery(id+"F7.wireOp",EDGE,"E75.trimOffspring"),sQuery(id+"F7.wireOp",EDGE,"E106")])]})]}),"instanceName":"1"})]}),makeQuery(id+"F22.opExtrude","SWEPT_FACE",FACE,{"disambiguationData":[OSD([sQuery(id+"F21.wireOp",EDGE,"E157.right")])]})]}),makeQuery(id+"F26.opExtrude","SWEPT_FACE",FACE,{"disambiguationData":[OSD([sQuery(id+"F25.wireOp",EDGE,"E289.right")])]})]});
            var sketch = newSketch(context, id + "F31", { "sketchPlane" : qUnion([Q0])});
            skLineSegment(sketch, "E306.bottom", {"start": v(600, 1475) * mm, "end": v(1600, 1475) * mm});
            skLineSegment(sketch, "E306.top", {"start": v(600, 725) * mm, "end": v(1600, 725) * mm});
            skLineSegment(sketch, "E306.left", {"start": v(600, 1475) * mm, "end": v(600, 725) * mm});
            skLineSegment(sketch, "E306.right", {"start": v(1600, 1475) * mm, "end": v(1600, 725) * mm});
            skLineSegment(sketch, "E307.bottom", {"start": v(4000, 1475) * mm, "end": v(5000, 1475) * mm});
            skLineSegment(sketch, "E307.top", {"start": v(4000, 725) * mm, "end": v(5000, 725) * mm});
            skLineSegment(sketch, "E307.left", {"start": v(4000, 1475) * mm, "end": v(4000, 725) * mm});
            skLineSegment(sketch, "E307.right", {"start": v(5000, 1475) * mm, "end": v(5000, 725) * mm});
            skLineSegment(sketch, "E308.bottom", {"start": v(600, 3775) * mm, "end": v(1600, 3775) * mm});
            skLineSegment(sketch, "E308.top", {"start": v(600, 4525) * mm, "end": v(1600, 4525) * mm});
            skLineSegment(sketch, "E308.left", {"start": v(600, 3775) * mm, "end": v(600, 4525) * mm});
            skLineSegment(sketch, "E308.right", {"start": v(1600, 3775) * mm, "end": v(1600, 4525) * mm});
            skLineSegment(sketch, "E309.bottom", {"start": v(4000, 3775) * mm, "end": v(5000, 3775) * mm});
            skLineSegment(sketch, "E309.top", {"start": v(4000, 4525) * mm, "end": v(5000, 4525) * mm});
            skLineSegment(sketch, "E309.left", {"start": v(4000, 3775) * mm, "end": v(4000, 4525) * mm});
            skLineSegment(sketch, "E309.right", {"start": v(5000, 3775) * mm, "end": v(5000, 4525) * mm});
            skSolve(sketch);
        }
        {
            var Q0;
            Q0 = qSketchRegion(id + "F31", true);
            extrude(context, id + "F32", {"entities" : qUnion([Q0]), "operationType" : NewBodyOperationType.REMOVE, "oppositeDirection" : true, "depth" : 50 * mm, "offsetDistance" : 25 * mm});
        }
    });
